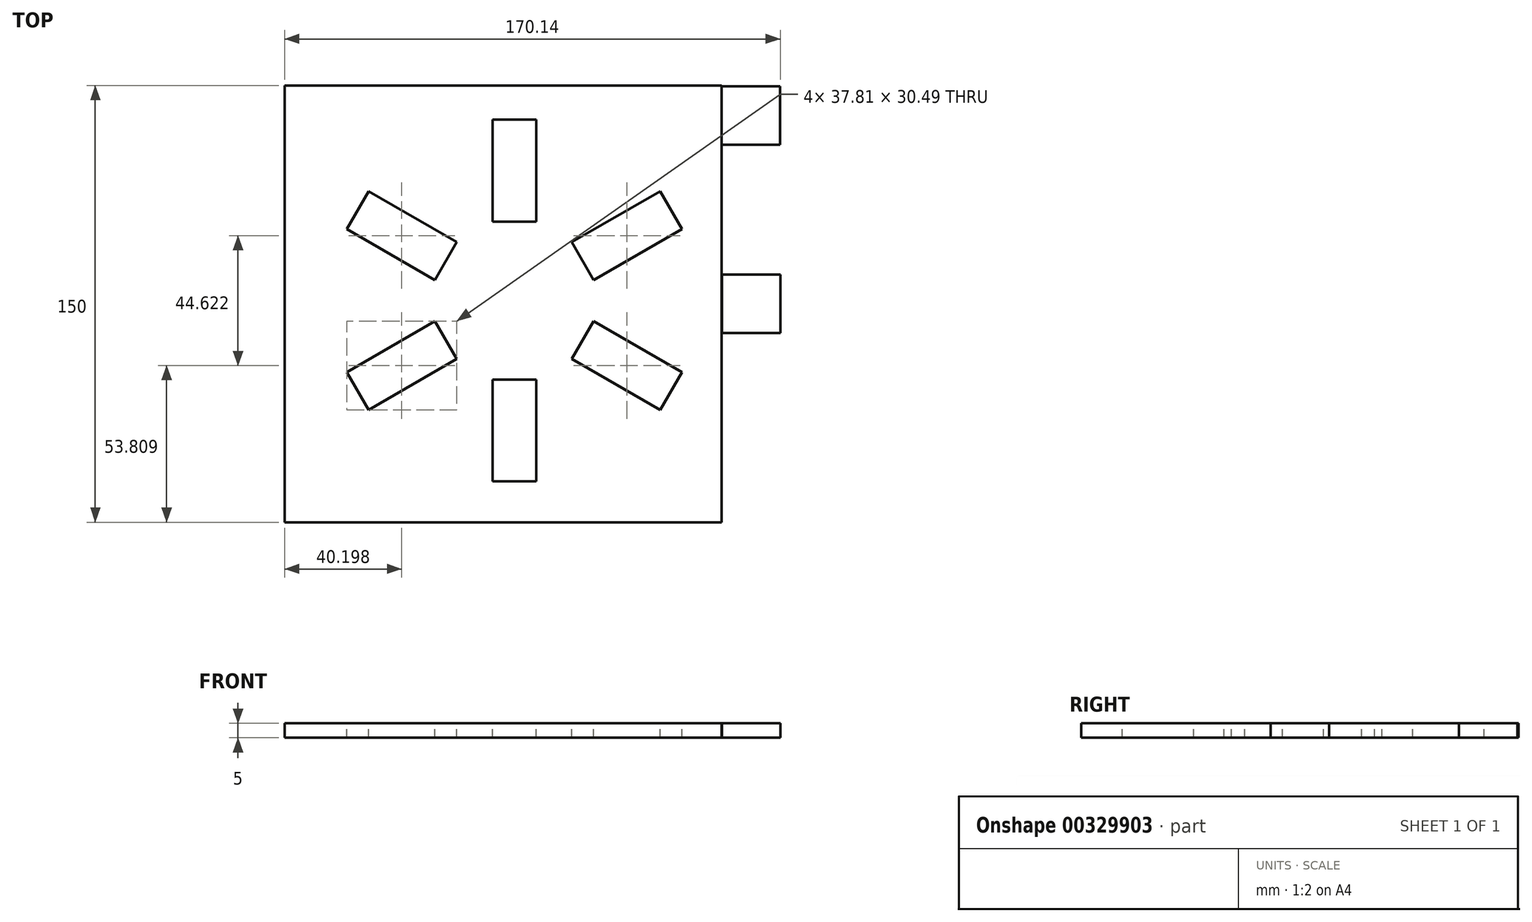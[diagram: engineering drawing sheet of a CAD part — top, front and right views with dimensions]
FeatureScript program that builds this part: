
annotation { "Feature Type Name" : "Feature", "Feature Type Description" : "" }
export const myFeature = defineFeature(function(context is Context, id is Id, definition is map)
    precondition{}
    {
        {
            var Q0;
            Q0=qCreatedBy(makeId("Top.planeOp"),FACE);
            var sketch = newSketch(context, id + "F0", { "sketchPlane" : qUnion([Q0])});
            skLineSegment(sketch, "E0.bottom", {"start": v(-78.67, 117.88) * mm, "end": v(71.33, 117.88) * mm});
            skLineSegment(sketch, "E0.top", {"start": v(-78.67, -32.12) * mm, "end": v(71.33, -32.12) * mm});
            skLineSegment(sketch, "E0.left", {"start": v(-78.67, 117.88) * mm, "end": v(-78.67, -32.12) * mm});
            skLineSegment(sketch, "E0.right", {"start": v(71.33, 117.88) * mm, "end": v(71.33, -32.12) * mm});
            skLineSegment(sketch, "E1.bottom", {"start": v(71.4, 117.52) * mm, "end": v(91.4, 117.52) * mm});
            skLineSegment(sketch, "E1.top", {"start": v(71.4, 97.52) * mm, "end": v(91.4, 97.52) * mm});
            skLineSegment(sketch, "E1.left", {"start": v(71.4, 117.52) * mm, "end": v(71.4, 97.52) * mm});
            skLineSegment(sketch, "E1.right", {"start": v(91.4, 117.52) * mm, "end": v(91.4, 97.52) * mm});
            skLineSegment(sketch, "E2.bottom", {"start": v(71.68, -11.28) * mm, "end": v(91.68, -11.28) * mm});
            skLineSegment(sketch, "E2.top", {"start": v(71.68, -31.28) * mm, "end": v(91.68, -31.28) * mm});
            skLineSegment(sketch, "E2.left", {"start": v(71.68, -11.28) * mm, "end": v(71.68, -31.28) * mm});
            skLineSegment(sketch, "E2.right", {"start": v(91.68, -11.28) * mm, "end": v(91.68, -31.28) * mm});
            skLineSegment(sketch, "E3.bottom", {"start": v(71.47, 52.88) * mm, "end": v(91.47, 52.88) * mm});
            skLineSegment(sketch, "E3.top", {"start": v(71.47, 32.88) * mm, "end": v(91.47, 32.88) * mm});
            skLineSegment(sketch, "E3.left", {"start": v(71.47, 52.88) * mm, "end": v(71.47, 32.88) * mm});
            skLineSegment(sketch, "E3.right", {"start": v(91.47, 52.88) * mm, "end": v(91.47, 32.88) * mm});
            skLineSegment(sketch, "E4", {"start": v(71.33, 117.88) * mm, "end": v(71.33, 52.88) * mm});
            skPoint(sketch, "E4.endSnap0", {"position": v(81.47, 52.88) * mm});
            skSolve(sketch);
        }
        {
            var Q0;
            Q0=makeQuery(id+"F0.imprint","IMPRINT",FACE,{"disambiguationData":[TD([[makeQuery(id+"F0.imprint","IMPRINT",EDGE,{"derivedFrom":sQuery(id+"F0.wireOp",EDGE,"E0.bottom")}),-1.0]])]});
            var Q1;
            Q1=makeQuery(id+"F0.imprint","IMPRINT",FACE,{"disambiguationData":[TD([[makeQuery(id+"F0.imprint","IMPRINT",EDGE,{"derivedFrom":sQuery(id+"F0.wireOp",EDGE,"E2.bottom")}),-1.0]])]});
            var Q2;
            Q2=makeQuery(id+"F0.imprint","IMPRINT",FACE,{"disambiguationData":[TD([[makeQuery(id+"F0.imprint","IMPRINT",EDGE,{"derivedFrom":sQuery(id+"F0.wireOp",EDGE,"E3.bottom")}),-1.0]])]});
            var Q3;
            Q3=makeQuery(id+"F0.imprint","IMPRINT",FACE,{"disambiguationData":[TD([[makeQuery(id+"F0.imprint","IMPRINT",EDGE,{"derivedFrom":sQuery(id+"F0.wireOp",EDGE,"E1.bottom")}),-1.0]])]});
            extrude(context, id + "F1", {"entities" : qUnion([Q0, Q1, Q2, Q3]), "depth" : 5 * mm});
        }
        {
            var Q0;
            Q0=makeQuery(id+"F1.opExtrude","CAP_FACE",FACE,{"disambiguationData":[OSD([sQuery(id+"F0.wireOp",EDGE,"E0.bottom"),sQuery(id+"F0.wireOp",EDGE,"E0.top"),sQuery(id+"F0.wireOp",EDGE,"E0.left"),sQuery(id+"F0.wireOp",EDGE,"E0.right"),sQuery(id+"F0.wireOp",EDGE,"E4")])],"isStart":false});
            var sketch = newSketch(context, id + "F2", { "sketchPlane" : qUnion([Q0])});
            skLineSegment(sketch, "E5.bottom", {"start": v(-7.33, 16.88) * mm, "end": v(7.67, 16.88) * mm});
            skLineSegment(sketch, "E5.top", {"start": v(-7.33, -18.12) * mm, "end": v(7.67, -18.12) * mm});
            skLineSegment(sketch, "E5.left", {"start": v(-7.33, 16.88) * mm, "end": v(-7.33, -18.12) * mm});
            skLineSegment(sketch, "E5.right", {"start": v(7.67, 16.88) * mm, "end": v(7.67, -18.12) * mm});
            skLineSegment(sketch, "E6.1.0", {"start": v(19.91, 23.94) * mm, "end": v(27.41, 36.93) * mm});
            skLineSegment(sketch, "E6.1.1", {"start": v(27.41, 36.93) * mm, "end": v(57.72, 19.43) * mm});
            skLineSegment(sketch, "E6.1.2", {"start": v(50.22, 6.44) * mm, "end": v(57.72, 19.43) * mm});
            skLineSegment(sketch, "E6.1.3", {"start": v(19.91, 23.94) * mm, "end": v(50.22, 6.44) * mm});
            skLineSegment(sketch, "E6.2.0", {"start": v(27.41, 51.07) * mm, "end": v(19.91, 64.06) * mm});
            skLineSegment(sketch, "E6.2.1", {"start": v(19.91, 64.06) * mm, "end": v(50.22, 81.56) * mm});
            skLineSegment(sketch, "E6.2.2", {"start": v(57.72, 68.57) * mm, "end": v(50.22, 81.56) * mm});
            skLineSegment(sketch, "E6.2.3", {"start": v(27.41, 51.07) * mm, "end": v(57.72, 68.57) * mm});
            skLineSegment(sketch, "E6.3.0", {"start": v(7.67, 71.12) * mm, "end": v(-7.33, 71.12) * mm});
            skLineSegment(sketch, "E6.3.1", {"start": v(-7.33, 71.12) * mm, "end": v(-7.33, 106.12) * mm});
            skLineSegment(sketch, "E6.3.2", {"start": v(7.67, 106.12) * mm, "end": v(-7.33, 106.12) * mm});
            skLineSegment(sketch, "E6.3.3", {"start": v(7.67, 71.12) * mm, "end": v(7.67, 106.12) * mm});
            skLineSegment(sketch, "E6.4.0", {"start": v(-19.57, 64.06) * mm, "end": v(-27.07, 51.07) * mm});
            skLineSegment(sketch, "E6.4.1", {"start": v(-27.07, 51.07) * mm, "end": v(-57.38, 68.57) * mm});
            skLineSegment(sketch, "E6.4.2", {"start": v(-49.88, 81.56) * mm, "end": v(-57.38, 68.57) * mm});
            skLineSegment(sketch, "E6.4.3", {"start": v(-19.57, 64.06) * mm, "end": v(-49.88, 81.56) * mm});
            skLineSegment(sketch, "E6.5.0", {"start": v(-27.07, 36.93) * mm, "end": v(-19.57, 23.94) * mm});
            skLineSegment(sketch, "E6.5.1", {"start": v(-19.57, 23.94) * mm, "end": v(-49.88, 6.44) * mm});
            skLineSegment(sketch, "E6.5.2", {"start": v(-57.38, 19.43) * mm, "end": v(-49.88, 6.44) * mm});
            skLineSegment(sketch, "E6.5.3", {"start": v(-27.07, 36.93) * mm, "end": v(-57.38, 19.43) * mm});
            skPoint(sketch, "E6.center", {"position": v(0.17, 44) * mm});
            skSolve(sketch);
        }
        {
            var Q0;
            Q0 = qSketchRegion(id + "F2", true);
            extrude(context, id + "F3", {"entities" : qUnion([Q0]), "operationType" : NewBodyOperationType.REMOVE, "oppositeDirection" : true, "depth" : 62 * mm});
        }
    });
